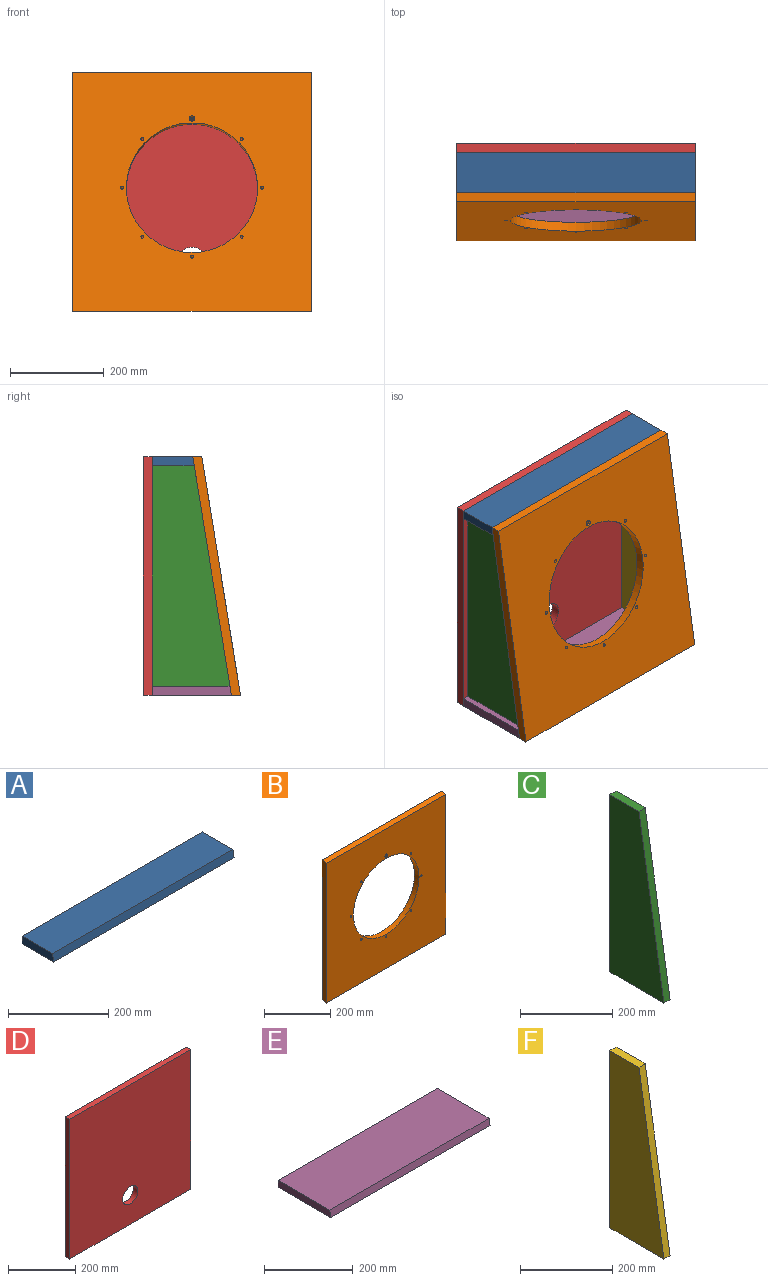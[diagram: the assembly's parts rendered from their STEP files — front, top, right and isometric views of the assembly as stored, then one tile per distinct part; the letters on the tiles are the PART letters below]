
ASSEMBLY  parts=6 mates=5
PART A: 6 faces, bbox 508x88.9x19.1 mm
  f0: plane 88.9x19.05mm, normal (1,0,0), area 1664.1mm2, adj f1,f3,f4,f5
  f1: plane 508x19.05mm, normal (0,1,0), area 9677.4mm2, adj f0,f2,f3,f4
  f2: plane 88.9x19.05mm, normal (-1,0,0), area 1664.1mm2, adj f1,f3,f4,f5
  f3: plane 508x85.81mm, normal (0,0,1), area 43592.2mm2, adj f0,f1,f2,f5
  f4: plane 508x88.9mm, normal (0,0,-1), area 45161.3mm2, adj f0,f1,f2,f5
  f5: plane 508x19.05mm, normal (0,-0.99,0.16), area 9803.8mm2, adj f0,f2,f3,f4
PART B: 16 faces, bbox 508x19.1x517.7 mm
  f0: plane 517.73x19.05mm, normal (-1,0,0), area 9804mm2, adj f1,f12,f13,f14
  f1: plane 508x19.05mm, normal (0,0.16,-0.99), area 9803.8mm2, adj f0,f2,f12,f13
  f2: plane 517.73x19.05mm, normal (1,0,0), area 9804mm2, adj f1,f12,f13,f14
  f3: cylinder r=3.17mm len=19.05mm, axis (0,1,0), area 380mm2, adj f12,f13
  f4: cylinder r=3.17mm len=19.05mm, axis (0,1,0), area 380mm2, adj f12,f13
  f5: cylinder r=3.17mm len=19.05mm, axis (0,1,0), area 380mm2, adj f12,f13
  f6: cylinder r=3.17mm len=19.05mm, axis (0,1,0), area 380mm2, adj f12,f13
  f7: cylinder r=3.17mm len=19.05mm, axis (0,1,0), area 380mm2, adj f12,f13
  f8: cylinder r=3.17mm len=16.51mm, axis (0,1,0), area 329.4mm2, adj f13,f15
  f9: cylinder r=3.17mm len=19.05mm, axis (0,1,0), area 380mm2, adj f12,f13
  f10: cylinder r=139.7mm len=279.4mm, axis (0,1,0), area 16721.3mm2, adj f12,f13
  f11: cylinder r=3.17mm len=19.05mm, axis (0,1,0), area 380mm2, adj f12,f13
  f12: plane 514.65x508mm, normal (0,-1,0), area 199803.9mm2, adj f0,f1,f2,f3,f4,f5,f6,f7
  f13: plane 514.65x508mm, normal (0,1,0), area 199874.8mm2, adj f0,f1,f2,f3,f4,f5,f6,f7
  f14: plane 508x19.05mm, normal (0,-0.16,0.99), area 9803.8mm2, adj f0,f2,f12,f13
  f15: cone r=3.17mm half-angle=45deg, axis (0,-1,0), area 100.3mm2, adj f8,f12
PART C: 6 faces, bbox 19.1x165.1x469.9 mm
  f0: plane 165.1x19.05mm, normal (0,0,-1), area 3145.2mm2, adj f1,f3,f4,f5
  f1: plane 469.9x19.05mm, normal (0,1,0), area 8951.6mm2, adj f0,f2,f4,f5
  f2: plane 88.9x19.05mm, normal (0,0,1), area 1693.5mm2, adj f1,f3,f4,f5
  f3: plane 469.9x76.2mm, normal (0,-0.99,0.16), area 9068.5mm2, adj f0,f2,f4,f5
  f4: plane 469.9x165.1mm, normal (1,0,0), area 59677.3mm2, adj f0,f1,f2,f3
  f5: plane 469.9x165.1mm, normal (-1,0,0), area 59677.3mm2, adj f0,f1,f2,f3
PART D: 7 faces, bbox 508x19.1x508 mm
  f0: plane 508x19.05mm, normal (-1,0,0), area 9677.4mm2, adj f1,f3,f5,f6
  f1: plane 508x19.05mm, normal (0,0,-1), area 9677.4mm2, adj f0,f2,f5,f6
  f2: plane 508x19.05mm, normal (1,0,0), area 9677.4mm2, adj f1,f3,f5,f6
  f3: plane 508x19.05mm, normal (0,0,1), area 9677.4mm2, adj f0,f2,f5,f6
  f4: cylinder r=31.75mm len=63.5mm, axis (0,1,0), area 3800.3mm2, adj f5,f6
  f5: plane 508x508mm, normal (0,-1,0), area 254897.1mm2, adj f0,f1,f2,f3,f4
  f6: plane 508x508mm, normal (0,1,0), area 254897.1mm2, adj f0,f1,f2,f3,f4
PART E: 6 faces, bbox 508x168.2x19.1 mm
  f0: plane 168.19x19.05mm, normal (1,0,0), area 3174.6mm2, adj f1,f3,f4,f5
  f1: plane 508x19.05mm, normal (0,1,0), area 9677.4mm2, adj f0,f2,f3,f4
  f2: plane 168.19x19.05mm, normal (-1,0,0), area 3174.6mm2, adj f1,f3,f4,f5
  f3: plane 508x165.1mm, normal (0,0,1), area 83870.8mm2, adj f0,f1,f2,f5
  f4: plane 508x168.19mm, normal (0,0,-1), area 85440.1mm2, adj f0,f1,f2,f5
  f5: plane 508x19.05mm, normal (0,-0.99,0.16), area 9803.8mm2, adj f0,f2,f3,f4
PART F: 6 faces, bbox 19.1x165.1x469.9 mm
  f0: plane 165.1x19.05mm, normal (0,0,-1), area 3145.2mm2, adj f1,f3,f4,f5
  f1: plane 469.9x19.05mm, normal (0,1,0), area 8951.6mm2, adj f0,f2,f4,f5
  f2: plane 88.9x19.05mm, normal (0,0,1), area 1693.5mm2, adj f1,f3,f4,f5
  f3: plane 469.9x76.2mm, normal (0,-0.99,0.16), area 9068.5mm2, adj f0,f2,f4,f5
  f4: plane 469.9x165.1mm, normal (1,0,0), area 59677.3mm2, adj f0,f1,f2,f3
  f5: plane 469.9x165.1mm, normal (-1,0,0), area 59677.3mm2, adj f0,f1,f2,f3
PLACE A t=(0,38.1,-155.62)mm
PLACE B rot(axis=(-1,0,0),9.2deg) t=(0,332.63,-64.44)mm
PLACE C t=(139.7,10.12,-9.53)mm
PLACE D t=(0,-248.85,-9.57)mm fixed
PLACE E t=(0,0,117.43)mm
PLACE F t=(-158.75,10.12,-9.53)mm
MATE fastened F.f1 <-> D.f5  axis (0,1,0) through (241.3,82.55,-9.57)mm
MATE fastened A.f1 <-> D.f5  axis (0,1,0) through (0,82.55,244.43)mm
MATE fastened B.f13 <-> F.f3  axis (0,0.99,-0.16) through (254,-44.45,-9.57)mm
MATE fastened D.f5 <-> E.f1  axis (0,-1,0) through (0,82.55,-263.57)mm
MATE fastened C.f1 <-> D.f5  axis (0,1,0) through (-241.3,82.55,-9.57)mm
